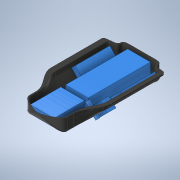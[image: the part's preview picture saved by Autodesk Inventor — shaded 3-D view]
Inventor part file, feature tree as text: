
AUTODESK INVENTOR PART (.ipt)
format: ipt  version: 2020.1 (Build 241239000, 239)  size: 2,054,656 bytes
history: native  units: mm
features: other x30, extrude x10, plane x8, loft x8, surface_op x7, sketch x5, delete_face x1, mirror x1
ambient origin geometry x8: Origin, YZ Plane, XZ Plane, XY Plane, X Axis, Y Axis, Z Axis, Center Point
bodies: Body1 (feature_tree), Body2 (feature_tree), Body3 (feature_tree), Body4 (feature_tree), Body5 (feature_tree), Body6 (feature_tree), Body7 (feature_tree), Body8 (feature_tree), Body9 (feature_tree), Body10 (feature_tree), Body11 (feature_tree), Body12 (feature_tree), Body13 (feature_tree), Body14 (feature_tree), Body15 (feature_tree), Body16 (feature_tree), Body17 (feature_tree)
feature tree (70):
  other  "deck.ipt"
  other  "Battery Pack"
  delete_face  "Delete Face1"
  surface_op  "Extend3"
  plane  "Work Plane1"
  extrude  "Battery Pack Volume"  Depth=300.0mm TaperAngle=0.0deg
  plane  "Work Plane2"
  extrude  "BMS, Anit-Spark, Reiceivers"  Depth=183.3mm
  plane  "Work Plane5"
  extrude  "Right VESC"  Depth=90.0mm TaperAngle=0.0deg
  mirror  "Left VESC"
  plane  "Work Plane3"
  extrude  "XLR Charging slot"  Depth=15.0mm
  extrude  "Power Button"  Depth=102.0mm TaperAngle=0.0deg
  plane  "Work Plane6"
  surface_op  "Extend4"
  other  "++++++ START OF BOX ++++++"
  plane  "Work Plane8"
  plane  "Work Plane9"
  plane  "Work Plane15"
  other  "BOX - Back Profile"
  other  "BOX - Front Profile"
  other  "BOX - End Profile"
  other  "Points"
  surface_op  "Stitch Surface4"
  surface_op  "Stitch Surface5"
  surface_op  "Trim3"
  surface_op  "Trim4"
  surface_op  "Sculpt6"
  other  "Srf1"
  sketch  "Sketch3"  dims[d2=10.0mm d3=300.0mm d4=0.0mm]
  sketch  "Sketch5"  dims[d6=67.0mm d7=183.3mm]
  sketch  "Sketch6"  dims[d8=37.0mm d9=0.0mm d13=90.0mm d14=0.0mm]
  sketch  "Sketch8"  dims[d15=135.0deg d16=15.0mm]
  sketch  "Sketch9"  dims[d17=40.0mm d18=102.0mm d19=0.0mm d20=-5.0mm d28=26.0mm d29=32.0mm d31=10.0mm d32=0.0mm d33=19.0mm d34=0.0mm d35=16.2mm d36=16.2mm d39=33.0mm d40=11.0mm d41=0.0mm d42=0.0mm d43=70.0mm d49=20.0mm d58=3.0mm d66=-41.0mm d67=5.0mm d68=12.0mm d69=-20.0mm d77=-20.0mm d78=0.0mm d79=12.0mm d83=6.0mm d88=2.0mm d91=3.0mm d92=10.0mm d93=3.0mm d94=2.0mm d97=150.0mm d98=0.0mm d99=20.0mm d100=0.0mm d110=33.5mm d126=10.0mm d140=21.0mm d151=5.0mm d178=3.0mm d179=4.0mm d182=3.0mm d183=3.0mm d185=5.0mm d186=2.0mm d187=3.0mm d200=150.0mm d201=0.0mm d202=20.0mm d203=0.0mm d212=7.0mm d213=90.0deg d220=10.0mm d221=90.0deg d222=10.0mm d223=90.0deg d224=15.0mm d225=90.0deg d226=10.0mm d227=90.0deg d240=10.0mm d241=90.0deg d242=20.0mm d243=90.0deg d248=10.0mm d249=90.0deg d250=11.0mm d251=90.0deg d257=30.0mm d258=8.0mm d259=15.0mm d260=11.0mm d263=12.0mm d264=6.0mm d265=3.0mm d266=23.0mm d269=6.0mm d270=6.0mm d271=4.0mm d272=10.0mm d273=90.0deg d274=25.0mm d275=90.0deg d278=10.0mm d279=90.0deg d280=5.0mm d281=90.0deg d282=3.0mm d283=-18.0mm d284=7.0mm d285=90.0deg d286=0.0mm d287=90.0deg d288=0.0mm d289=90.0deg d290=105.0mm d291=7.417649mm]
  other  "Front Profile"
  other  "Srf2"
  other  "Srf3"
  other  "Srf16"
  other  "Srf17"
  other  "Srf20"
  other  "Srf21"
  other  "Srf22"
  other  "Srf23"
  other  "Edges15"
  other  "Edges16"
  other  "Edges13"
  other  "Edges14"
  other  "Srf26"
  other  "Srf27"
  other  "Srf28"
  other  "Srf29"
  other  "Srf30"
  other  "Srf31"
  other  "Edges17"
  other  "Edges18"
  other  "Box"
  extrude  "ExtrusionSrf1"  [1 undecoded]
  extrude  "ExtrusionSrf2"  Depth=26.0mm
  extrude  "ExtrusionSrf3"  Depth=32.0mm
  extrude  "ExtrusionSrf7"  Depth=10.0mm TaperAngle=0.0deg
  extrude  "ExtrusionSrf8"  Depth=19.0mm TaperAngle=0.0deg
  loft  "LoftSrf8"
  loft  "LoftSrf9"
  loft  "LoftSrf10"
  loft  "LoftSrf11"
  loft  "LoftSrf12"
  loft  "LoftSrf13"
  loft  "LoftSrf14"
  loft  "LoftSrf15"
note: 1 required parameter value undecoded (feature->parameter linkage not recoverable at this tier; creation-order binding heuristic only, values carry confidence <= 0.55)
